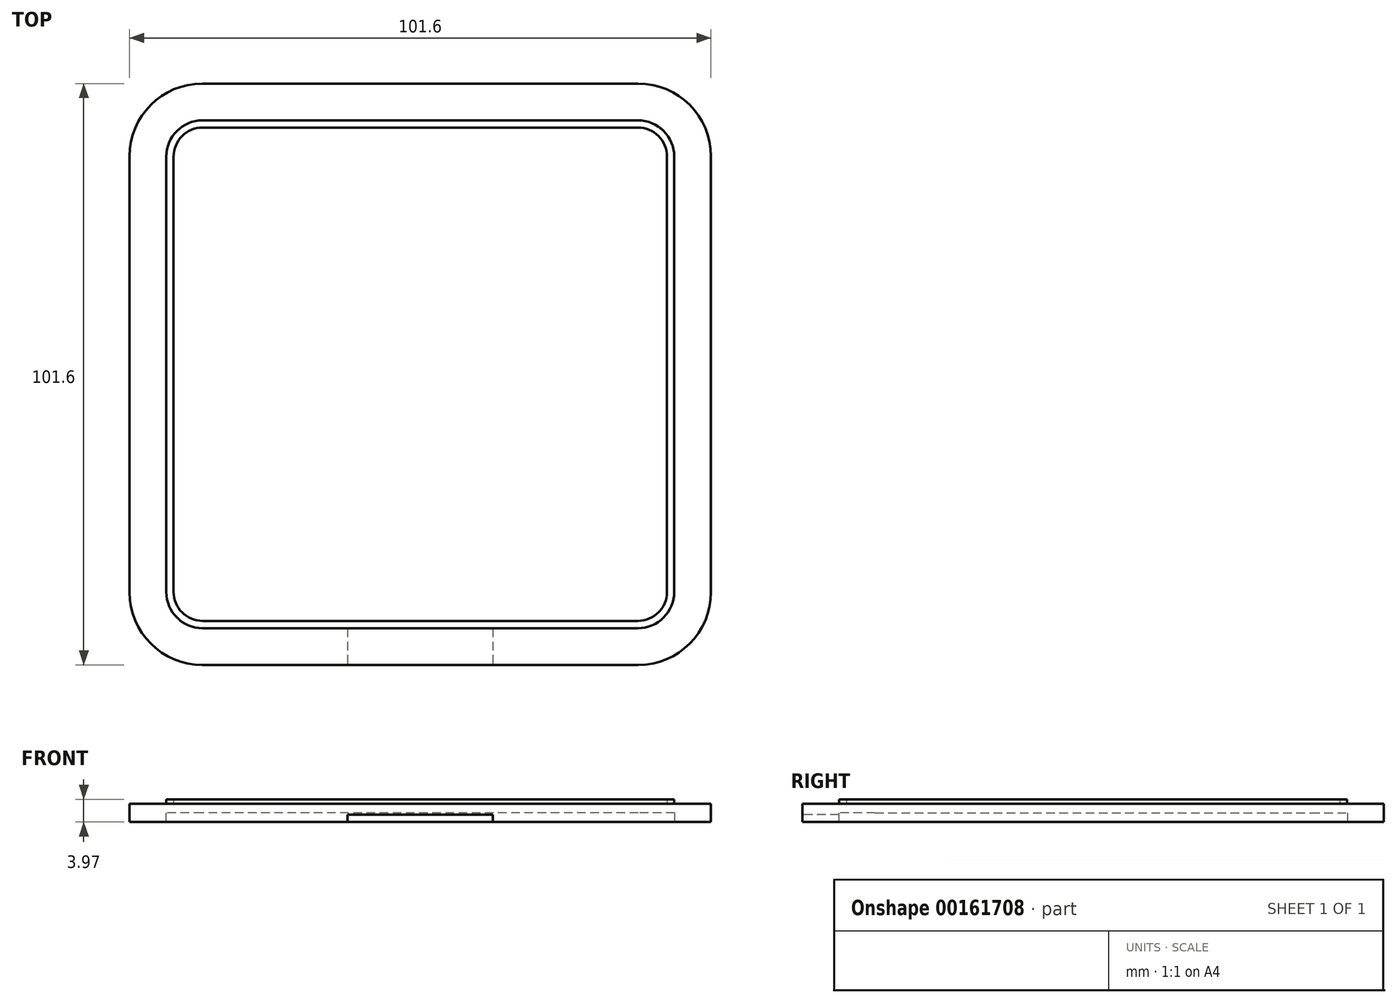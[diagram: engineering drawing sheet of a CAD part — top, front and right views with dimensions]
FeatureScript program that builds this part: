
annotation { "Feature Type Name" : "Feature", "Feature Type Description" : "" }
export const myFeature = defineFeature(function(context is Context, id is Id, definition is map)
    precondition{}
    {
        {
            var Q0;
            Q0=qCreatedBy(makeId("Top.planeOp"),FACE);
            var sketch = newSketch(context, id + "F0", { "sketchPlane" : qUnion([Q0])});
            skLineSegment(sketch, "E0.bottom", {"start": v(38.1, 50.8) * mm, "end": v(-38.1, 50.8) * mm});
            skLineSegment(sketch, "E0.top", {"start": v(38.1, -50.8) * mm, "end": v(-38.1, -50.8) * mm});
            skLineSegment(sketch, "E0.left", {"start": v(50.8, 38.1) * mm, "end": v(50.8, -38.1) * mm});
            skLineSegment(sketch, "E0.right", {"start": v(-50.8, 38.1) * mm, "end": v(-50.8, -38.1) * mm});
            skPoint(sketch, "E0.middle", {"position": v(0, 0) * mm});
            skPoint(sketch, "E1.visualSharp", {"position": v(50.8, 50.8) * mm});
            skArc(sketch, "E1.filletArc", {"start": v(50.8, 38.1) * mm, "mid": v(47.08, 47.08) * mm, "end": v(38.1, 50.8) * mm});
            skPoint(sketch, "E2.visualSharp", {"position": v(50.8, -50.8) * mm});
            skArc(sketch, "E2.filletArc", {"start": v(38.1, -50.8) * mm, "mid": v(47.08, -47.08) * mm, "end": v(50.8, -38.1) * mm});
            skPoint(sketch, "E3.visualSharp", {"position": v(-50.8, -50.8) * mm});
            skArc(sketch, "E3.filletArc", {"start": v(-50.8, -38.1) * mm, "mid": v(-47.08, -47.08) * mm, "end": v(-38.1, -50.8) * mm});
            skPoint(sketch, "E4.visualSharp", {"position": v(-50.8, 50.8) * mm});
            skArc(sketch, "E4.filletArc", {"start": v(-38.1, 50.8) * mm, "mid": v(-47.08, 47.08) * mm, "end": v(-50.8, 38.1) * mm});
            skSolve(sketch);
        }
        {
            var Q0;
            Q0=makeQuery(id+"F0.imprint","IMPRINT",FACE,{"disambiguationData":[TD([[makeQuery(id+"F0.imprint","IMPRINT",EDGE,{"derivedFrom":sQuery(id+"F0.wireOp",EDGE,"E0.bottom")}),1.0]])]});
            extrude(context, id + "F1", {"entities" : qUnion([Q0]), "depth" : 3.17 * mm});
        }
        {
            var Q0;
            Q0=makeQuery(id+"F1.opExtrude","CAP_FACE",FACE,{"disambiguationData":[OSD([sQuery(id+"F0.wireOp",EDGE,"E0.bottom"),sQuery(id+"F0.wireOp",EDGE,"E0.top"),sQuery(id+"F0.wireOp",EDGE,"E0.left"),sQuery(id+"F0.wireOp",EDGE,"E0.right"),sQuery(id+"F0.wireOp",EDGE,"E1.filletArc"),sQuery(id+"F0.wireOp",EDGE,"E2.filletArc"),sQuery(id+"F0.wireOp",EDGE,"E3.filletArc"),sQuery(id+"F0.wireOp",EDGE,"E4.filletArc")])],"isStart":true});
            var sketch = newSketch(context, id + "F2", { "sketchPlane" : qUnion([Q0])});
            skLineSegment(sketch, "E5.bottom", {"start": v(38.1, 44.45) * mm, "end": v(-38.1, 44.45) * mm});
            skLineSegment(sketch, "E5.top", {"start": v(38.1, -44.45) * mm, "end": v(-38.1, -44.45) * mm});
            skLineSegment(sketch, "E5.left", {"start": v(44.45, 38.1) * mm, "end": v(44.45, -38.1) * mm});
            skLineSegment(sketch, "E5.right", {"start": v(-44.45, 38.1) * mm, "end": v(-44.45, -38.1) * mm});
            skPoint(sketch, "E5.middle", {"position": v(0, 0) * mm});
            skPoint(sketch, "E6.visualSharp", {"position": v(-44.45, 44.45) * mm});
            skArc(sketch, "E6.filletArc", {"start": v(-38.1, 44.45) * mm, "mid": v(-42.6, 42.6) * mm, "end": v(-44.45, 38.1) * mm});
            skPoint(sketch, "E7.visualSharp", {"position": v(44.45, 44.45) * mm});
            skArc(sketch, "E7.filletArc", {"start": v(44.45, 38.1) * mm, "mid": v(42.6, 42.6) * mm, "end": v(38.1, 44.45) * mm});
            skPoint(sketch, "E8.visualSharp", {"position": v(44.45, -44.45) * mm});
            skArc(sketch, "E8.filletArc", {"start": v(38.1, -44.45) * mm, "mid": v(42.6, -42.6) * mm, "end": v(44.45, -38.1) * mm});
            skPoint(sketch, "E9.visualSharp", {"position": v(-44.45, -44.45) * mm});
            skArc(sketch, "E9.filletArc", {"start": v(-44.45, -38.1) * mm, "mid": v(-42.6, -42.6) * mm, "end": v(-38.1, -44.45) * mm});
            skSolve(sketch);
        }
        {
            var Q0;
            Q0=makeQuery(id+"F2.imprint","IMPRINT",FACE,{"disambiguationData":[TD([[makeQuery(id+"F2.imprint","IMPRINT",EDGE,{"derivedFrom":sQuery(id+"F2.wireOp",EDGE,"E5.bottom")}),1.0]])]});
            extrude(context, id + "F3", {"entities" : qUnion([Q0]), "operationType" : NewBodyOperationType.REMOVE, "oppositeDirection" : true, "depth" : 1.59 * mm});
        }
        {
            var Q0;
            Q0=makeQuery(id+"F1.opExtrude","SWEPT_FACE",FACE,{"disambiguationData":[OSD([sQuery(id+"F0.wireOp",EDGE,"E0.top")])]});
            var sketch = newSketch(context, id + "F4", { "sketchPlane" : qUnion([Q0])});
            skLineSegment(sketch, "E10.bottom", {"start": v(12.7, 1.27) * mm, "end": v(-12.7, 1.27) * mm});
            skLineSegment(sketch, "E10.top", {"start": v(12.7, -1.27) * mm, "end": v(-12.7, -1.27) * mm});
            skLineSegment(sketch, "E10.left", {"start": v(12.7, 1.27) * mm, "end": v(12.7, -1.27) * mm});
            skLineSegment(sketch, "E10.right", {"start": v(-12.7, 1.27) * mm, "end": v(-12.7, -1.27) * mm});
            skPoint(sketch, "E10.middle", {"position": v(0, 0) * mm});
            skSolve(sketch);
        }
        {
            var Q0;
            {var subQ0=sQuery(id+"F4.wireOp",EDGE,"E10.bottom");Q0=makeQuery(id+"F4.imprint","IMPRINT",FACE,{"disambiguationData":[TD([[makeQuery(id+"F4.imprint","IMPRINT",EDGE,{"derivedFrom":subQ0}),1.0]])]});}
            var Q1;
            {var subQ0=sQuery(id+"F4.wireOp",EDGE,"E10.top");Q1=makeQuery(id+"F4.imprint","IMPRINT",FACE,{"disambiguationData":[TD([[makeQuery(id+"F4.imprint","IMPRINT",EDGE,{"derivedFrom":subQ0}),-1.0]])]});}
            extrude(context, id + "F5", {"entities" : qUnion([Q0, Q1]), "operationType" : NewBodyOperationType.REMOVE, "oppositeDirection" : true, "depth" : 25.4 * mm});
        }
        {
            var Q0;
            Q0=makeQuery(id+"F1.opExtrude","CAP_FACE",FACE,{"disambiguationData":[OSD([sQuery(id+"F0.wireOp",EDGE,"E0.bottom"),sQuery(id+"F0.wireOp",EDGE,"E0.top"),sQuery(id+"F0.wireOp",EDGE,"E0.left"),sQuery(id+"F0.wireOp",EDGE,"E0.right"),sQuery(id+"F0.wireOp",EDGE,"E1.filletArc"),sQuery(id+"F0.wireOp",EDGE,"E2.filletArc"),sQuery(id+"F0.wireOp",EDGE,"E3.filletArc"),sQuery(id+"F0.wireOp",EDGE,"E4.filletArc")])],"isStart":false});
            var sketch = newSketch(context, id + "F6", { "sketchPlane" : qUnion([Q0])});
            skLineSegment(sketch, "E11.bottom", {"start": v(38.04, -44.39) * mm, "end": v(-38.04, -44.39) * mm});
            skLineSegment(sketch, "E11.top", {"start": v(38.04, 44.39) * mm, "end": v(-38.04, 44.39) * mm});
            skLineSegment(sketch, "E11.left", {"start": v(44.39, -38.04) * mm, "end": v(44.39, 38.04) * mm});
            skLineSegment(sketch, "E11.right", {"start": v(-44.39, -38.04) * mm, "end": v(-44.39, 38.04) * mm});
            skPoint(sketch, "E11.middle", {"position": v(0, 0) * mm});
            skPoint(sketch, "E12.visualSharp", {"position": v(-44.39, 44.39) * mm});
            skArc(sketch, "E12.filletArc", {"start": v(-38.04, 44.39) * mm, "mid": v(-42.53, 42.53) * mm, "end": v(-44.39, 38.04) * mm});
            skPoint(sketch, "E13.visualSharp", {"position": v(44.39, 44.39) * mm});
            skArc(sketch, "E13.filletArc", {"start": v(44.39, 38.04) * mm, "mid": v(42.53, 42.53) * mm, "end": v(38.04, 44.39) * mm});
            skPoint(sketch, "E14.visualSharp", {"position": v(44.39, -44.39) * mm});
            skArc(sketch, "E14.filletArc", {"start": v(38.04, -44.39) * mm, "mid": v(42.53, -42.53) * mm, "end": v(44.39, -38.04) * mm});
            skPoint(sketch, "E15.visualSharp", {"position": v(-44.39, -44.39) * mm});
            skArc(sketch, "E15.filletArc", {"start": v(-44.39, -38.04) * mm, "mid": v(-42.53, -42.53) * mm, "end": v(-38.04, -44.39) * mm});
            skArc(sketch, "E16.0", {"start": v(43.12, 38.04) * mm, "mid": v(41.63, 41.63) * mm, "end": v(38.04, 43.12) * mm});
            skLineSegment(sketch, "E16.1", {"start": v(43.12, -38.04) * mm, "end": v(43.12, 38.04) * mm});
            skLineSegment(sketch, "E16.2", {"start": v(38.04, 43.12) * mm, "end": v(-38.04, 43.12) * mm});
            skArc(sketch, "E16.3", {"start": v(38.04, -43.12) * mm, "mid": v(41.63, -41.63) * mm, "end": v(43.12, -38.04) * mm});
            skArc(sketch, "E16.4", {"start": v(-38.04, 43.12) * mm, "mid": v(-41.63, 41.63) * mm, "end": v(-43.12, 38.04) * mm});
            skLineSegment(sketch, "E16.5", {"start": v(-43.12, -38.04) * mm, "end": v(-43.12, 38.04) * mm});
            skArc(sketch, "E16.6", {"start": v(-43.12, -38.04) * mm, "mid": v(-41.63, -41.63) * mm, "end": v(-38.04, -43.12) * mm});
            skLineSegment(sketch, "E16.7", {"start": v(38.04, -43.12) * mm, "end": v(-38.04, -43.12) * mm});
            skSolve(sketch);
        }
        {
            var Q0;
            Q0=makeQuery(id+"F6.imprint","IMPRINT",FACE,{"disambiguationData":[TD([[makeQuery(id+"F6.imprint","IMPRINT",EDGE,{"derivedFrom":sQuery(id+"F6.wireOp",EDGE,"E11.bottom")}),-1.0]])]});
            extrude(context, id + "F7", {"entities" : qUnion([Q0]), "operationType" : NewBodyOperationType.ADD, "depth" : 0.8 * mm});
        }
    });
